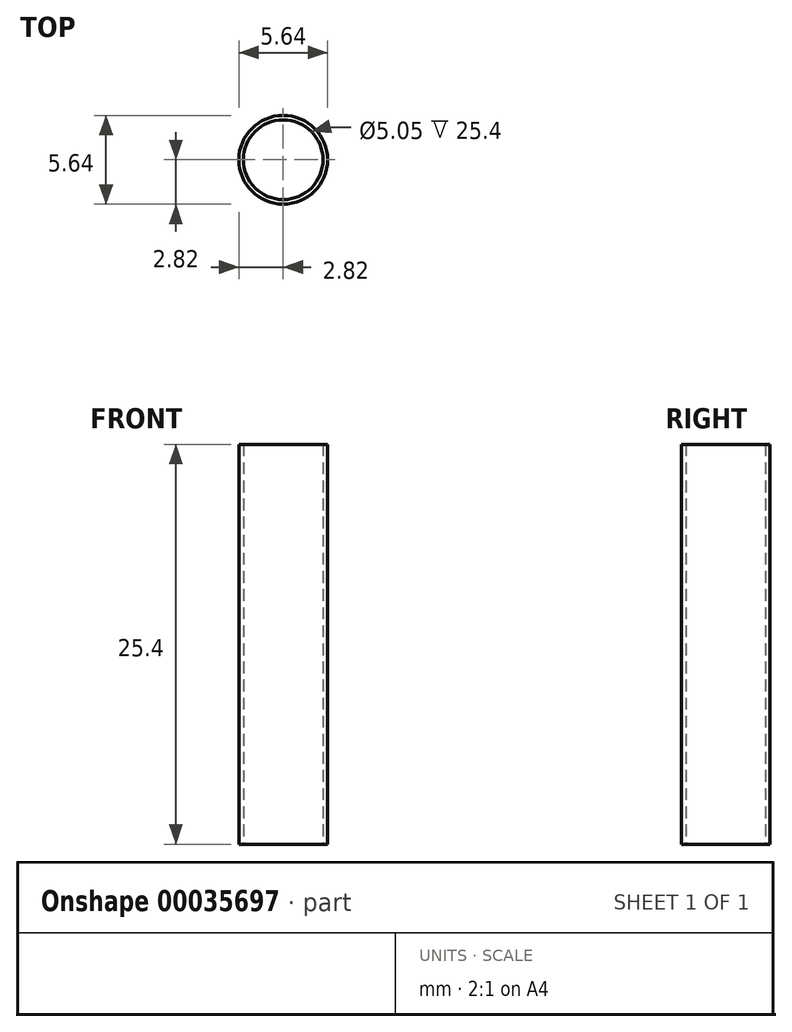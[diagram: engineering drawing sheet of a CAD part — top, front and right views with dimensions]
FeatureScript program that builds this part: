
annotation { "Feature Type Name" : "Feature", "Feature Type Description" : "" }
export const myFeature = defineFeature(function(context is Context, id is Id, definition is map)
    precondition{}
    {
        {
            var Q0;
            Q0=qCreatedBy(makeId("Front.planeOp"),FACE);
            var sketch = newSketch(context, id + "F0", { "sketchPlane" : qUnion([Q0])});
            skLineSegment(sketch, "E0", {"start": v(0, 0) * mm, "end": v(0, 25.4) * mm});
            skLineSegment(sketch, "E1", {"start": v(0, 25.4) * mm, "end": v(2.53, 25.4) * mm});
            skLineSegment(sketch, "E2", {"start": v(2.53, 25.4) * mm, "end": v(2.53, 0) * mm});
            skLineSegment(sketch, "E3", {"start": v(2.53, 0) * mm, "end": v(0, 0) * mm});
            skLineSegment(sketch, "E4", {"start": v(2.53, 0) * mm, "end": v(2.82, 0) * mm});
            skLineSegment(sketch, "E5", {"start": v(2.82, 0) * mm, "end": v(2.82, 25.4) * mm});
            skLineSegment(sketch, "E6", {"start": v(2.82, 25.4) * mm, "end": v(2.53, 25.4) * mm});
            skSolve(sketch);
        }
        {
            var Q0;
            Q0=makeQuery(id+"F0.imprint","IMPRINT",FACE,{"disambiguationData":[TD([[makeQuery(id+"F0.imprint","IMPRINT",EDGE,{"derivedFrom":sQuery(id+"F0.wireOp",EDGE,"E2")}),1.0]])]});
            var Q1;
            Q1=sQuery(id+"F0.wireOp",EDGE,"E0");
            revolve(context, id + "F1", {"entities" : qUnion([Q0]), "axis" : qUnion([Q1]), "revolveType" : RevolveType.FULL});
        }
    });
